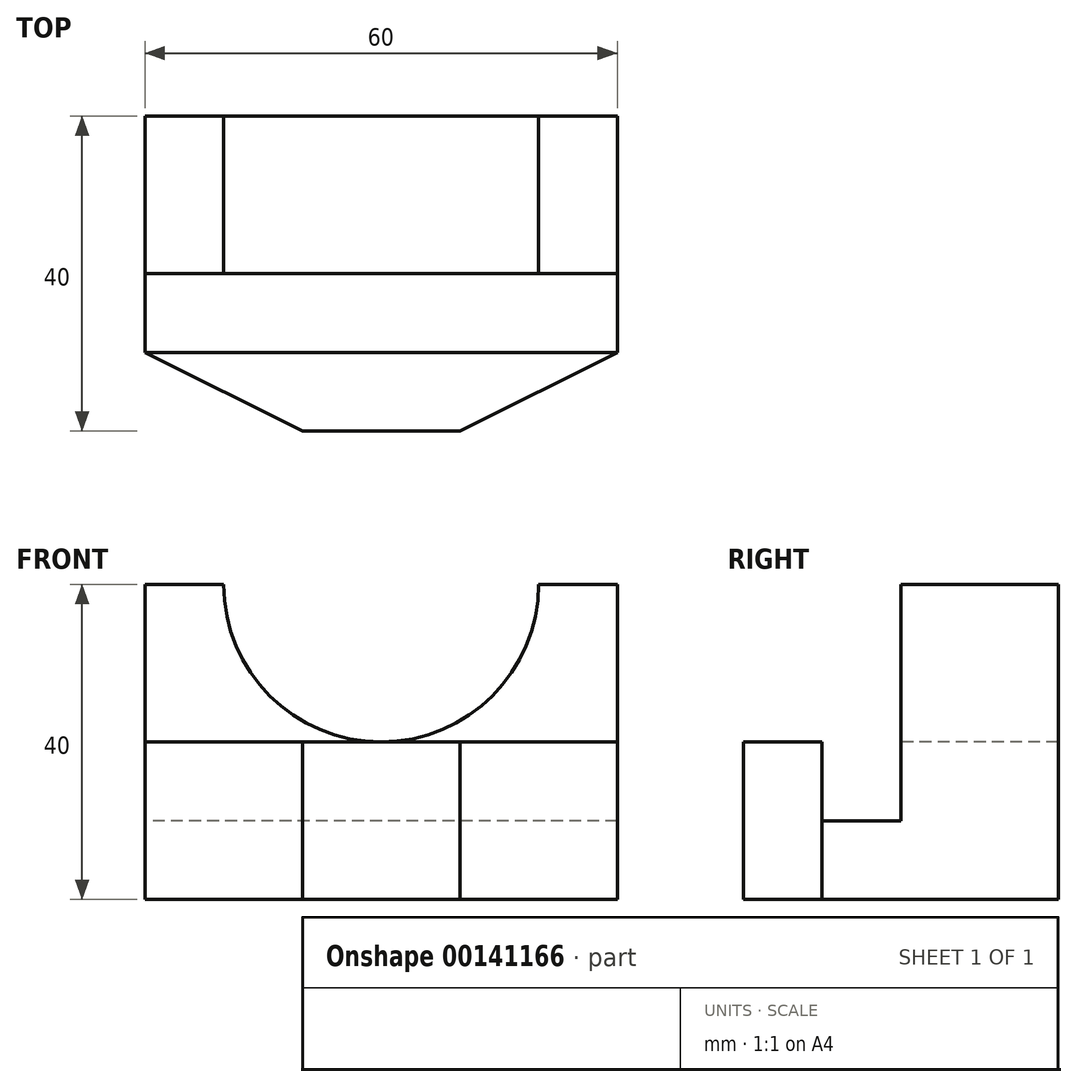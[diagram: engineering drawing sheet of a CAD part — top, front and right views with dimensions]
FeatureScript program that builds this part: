
annotation { "Feature Type Name" : "Feature", "Feature Type Description" : "" }
export const myFeature = defineFeature(function(context is Context, id is Id, definition is map)
    precondition{}
    {
        {
            var Q0;
            Q0=qCreatedBy(makeId("Top.planeOp"),FACE);
            var sketch = newSketch(context, id + "F0", { "sketchPlane" : qUnion([Q0])});
            skLineSegment(sketch, "E0", {"start": v(0, 0) * mm, "end": v(0, 20) * mm});
            skLineSegment(sketch, "E1", {"start": v(0, 20) * mm, "end": v(60, 20) * mm});
            skLineSegment(sketch, "E2", {"start": v(60, 20) * mm, "end": v(60, 0) * mm});
            skLineSegment(sketch, "E3", {"start": v(60, 0) * mm, "end": v(0, 0) * mm});
            skLineSegment(sketch, "E4", {"start": v(0, 0) * mm, "end": v(0, -10) * mm});
            skLineSegment(sketch, "E5", {"start": v(0, -10) * mm, "end": v(60, -10) * mm});
            skLineSegment(sketch, "E6", {"start": v(60, -10) * mm, "end": v(60, 0) * mm});
            skLineSegment(sketch, "E7", {"start": v(0, -10) * mm, "end": v(20, -20) * mm});
            skLineSegment(sketch, "E8", {"start": v(20, -20) * mm, "end": v(40, -20) * mm});
            skLineSegment(sketch, "E9", {"start": v(40, -20) * mm, "end": v(60, -10) * mm});
            skSolve(sketch);
        }
        {
            var Q0;
            Q0=makeQuery(id+"F0.imprint","IMPRINT",FACE,{"disambiguationData":[TD([[makeQuery(id+"F0.imprint","IMPRINT",EDGE,{"derivedFrom":sQuery(id+"F0.wireOp",EDGE,"E0")}),-1.0]])]});
            extrude(context, id + "F1", {"entities" : qUnion([Q0]), "depth" : 40 * mm});
        }
        {
            var Q0;
            Q0=makeQuery(id+"F0.imprint","IMPRINT",FACE,{"disambiguationData":[TD([[makeQuery(id+"F0.imprint","IMPRINT",EDGE,{"derivedFrom":sQuery(id+"F0.wireOp",EDGE,"E3")}),1.0]])]});
            extrude(context, id + "F2", {"entities" : qUnion([Q0]), "operationType" : NewBodyOperationType.ADD, "depth" : 10 * mm});
        }
        {
            var Q0;
            Q0=makeQuery(id+"F0.imprint","IMPRINT",FACE,{"disambiguationData":[TD([[makeQuery(id+"F0.imprint","IMPRINT",EDGE,{"derivedFrom":sQuery(id+"F0.wireOp",EDGE,"E5")}),-1.0]])]});
            extrude(context, id + "F3", {"entities" : qUnion([Q0]), "operationType" : NewBodyOperationType.ADD, "depth" : 20 * mm});
        }
        {
            var Q0;
            Q0=makeQuery(id+"F1.opExtrude","SWEPT_FACE",FACE,{"disambiguationData":[OSD([sQuery(id+"F0.wireOp",EDGE,"E3")])]});
            var sketch = newSketch(context, id + "F4", { "sketchPlane" : qUnion([Q0])});
            skArc(sketch, "E10", {"start": v(10, 40) * mm, "mid": v(30, 20) * mm, "end": v(50, 40) * mm});
            skLineSegment(sketch, "E11", {"start": v(10, 40) * mm, "end": v(50, 40) * mm});
            skSolve(sketch);
        }
        {
            var Q0;
            Q0 = qSketchRegion(id + "F4", true);
            extrude(context, id + "F5", {"entities" : qUnion([Q0]), "operationType" : NewBodyOperationType.REMOVE, "endBound" : BoundingType.THROUGH_ALL, "oppositeDirection" : true, "depth" : 25 * mm});
        }
    });
